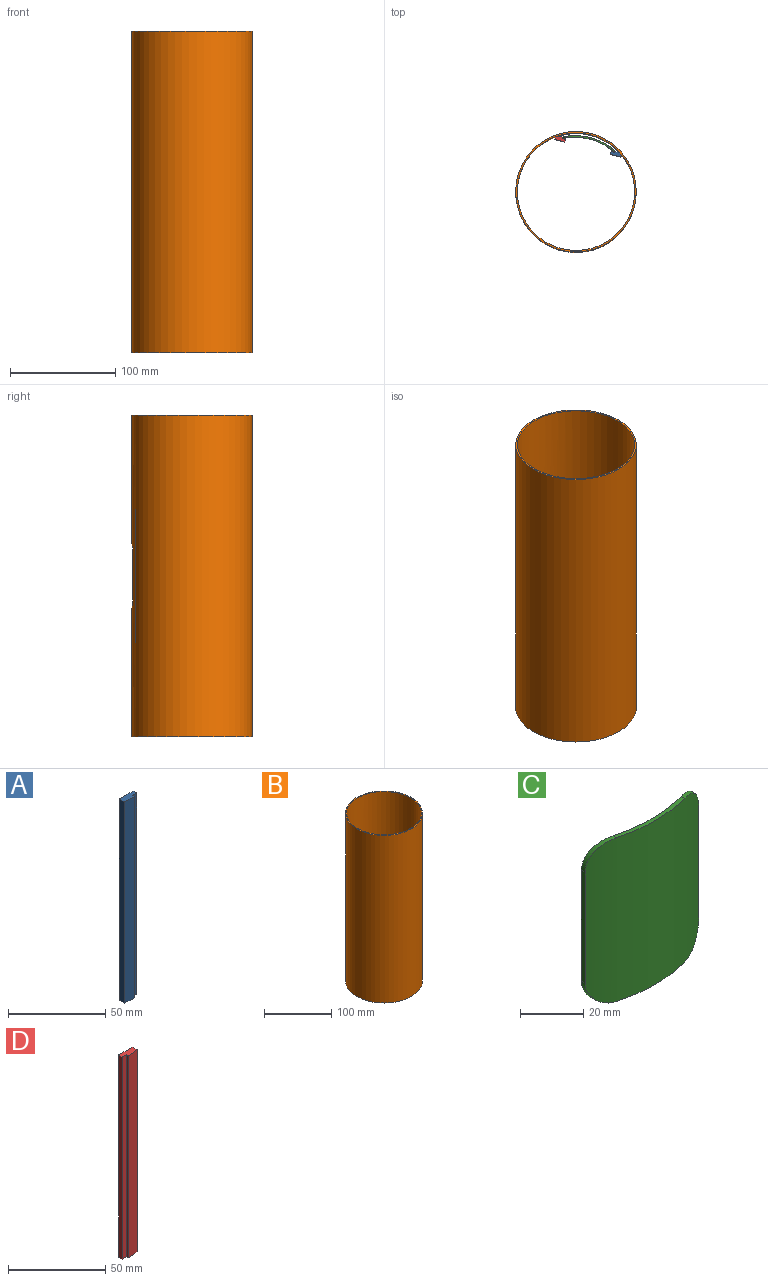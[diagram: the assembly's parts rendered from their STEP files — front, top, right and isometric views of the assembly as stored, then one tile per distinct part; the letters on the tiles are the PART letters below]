
ASSEMBLY  parts=4 mates=3
PART A: 8 faces, bbox 10x4x127 mm
  f0: plane 127x2.5mm, normal (1,0,0), area 317.5mm2, adj f1,f5,f6,f7
  f1: plane 127x10mm, normal (0,1,0), area 1270mm2, adj f0,f2,f6,f7
  f2: plane 127x3.56mm, normal (-1,0,0), area 451.9mm2, adj f1,f3,f6,f7
  f3: cylinder r=55.65mm len=127mm, axis (0,0,-1), area 891.4mm2, adj f2,f4,f6,f7
  f4: plane 127x1.5mm, normal (1,0,0), area 190.5mm2, adj f3,f5,f6,f7
  f5: plane 127x3mm, normal (0,-1,0), area 381mm2, adj f0,f4,f6,f7
  f6: plane 10x4mm, normal (0,0,1), area 34.5mm2, adj f0,f1,f2,f3,f4,f5
  f7: plane 10x4mm, normal (0,0,-1), area 34.5mm2, adj f0,f1,f2,f3,f4,f5
PART B: 12 faces, bbox 114.3x114.3x304.8 mm
  f0: cylinder r=55.65mm len=304.8mm, axis (0,0,-1), area 103323.9mm2, adj f2,f3,f4,f5,f6,f7,f8,f9
  f1: cylinder r=57.15mm len=304.8mm, axis (0,0,-1), area 106203.1mm2, adj f2,f3,f4,f5,f6,f7,f8,f9
  f2: plane 114.3x114.3mm, normal (0,0,1), area 531.6mm2, adj f0,f1
  f3: plane 114.3x114.3mm, normal (0,0,-1), area 531.6mm2, adj f0,f1
  f4: plane 30.48x3.63mm, normal (0,0,-1), area 46.3mm2, adj f0,f1,f5,f11
  f5: cylinder r=10.16mm len=10.16mm, axis (0,-1,0), area 26mm2, adj f0,f1,f4,f6
  f6: plane 43.18x1.68mm, normal (1,0,0), area 72.5mm2, adj f0,f1,f5,f7
  f7: cylinder r=10.16mm len=10.16mm, axis (0,-1,0), area 26mm2, adj f0,f1,f6,f8
  f8: plane 30.48x3.63mm, normal (0,0,1), area 46.3mm2, adj f0,f1,f7,f9
  f9: cylinder r=10.16mm len=10.16mm, axis (0,-1,0), area 26mm2, adj f0,f1,f8,f10
  f10: plane 43.18x1.68mm, normal (-1,0,0), area 72.5mm2, adj f0,f1,f9,f11
  f11: cylinder r=10.16mm len=10.16mm, axis (0,-1,0), area 26mm2, adj f0,f1,f4,f10
PART C: 10 faces, bbox 50.8x7.6x63.5 mm
  f0: plane 30.48x3.63mm, normal (0,0,1), area 46.3mm2, adj f2,f7,f8,f9
  f1: plane 30.48x3.63mm, normal (0,0,-1), area 46.3mm2, adj f4,f5,f8,f9
  f2: cylinder r=10.16mm len=10.16mm, axis (0,-1,0), area 26mm2, adj f0,f3,f8,f9
  f3: plane 43.18x1.68mm, normal (-1,0,0), area 72.5mm2, adj f2,f4,f8,f9
  f4: cylinder r=10.16mm len=10.16mm, axis (0,-1,0), area 26mm2, adj f1,f3,f8,f9
  f5: cylinder r=10.16mm len=10.16mm, axis (0,-1,0), area 26mm2, adj f1,f6,f8,f9
  f6: plane 43.18x1.68mm, normal (1,0,0), area 72.5mm2, adj f5,f7,f8,f9
  f7: cylinder r=10.16mm len=10.16mm, axis (0,-1,0), area 26mm2, adj f0,f6,f8,f9
  f8: cylinder r=55.65mm len=63.5mm, axis (0,0,-1), area 3252.3mm2, adj f0,f1,f2,f3,f4,f5,f6,f7
  f9: cylinder r=57.15mm len=63.5mm, axis (0,0,-1), area 3245.7mm2, adj f0,f1,f2,f3,f4,f5,f6,f7
PART D: 8 faces, bbox 10x4x127 mm
  f0: plane 127x1.5mm, normal (-1,0,0), area 190.5mm2, adj f1,f5,f6,f7
  f1: cylinder r=55.65mm len=127mm, axis (0,0,-1), area 891.4mm2, adj f0,f2,f6,f7
  f2: plane 127x3.56mm, normal (1,0,0), area 451.9mm2, adj f1,f3,f6,f7
  f3: plane 127x10mm, normal (0,1,0), area 1270mm2, adj f2,f4,f6,f7
  f4: plane 127x2.5mm, normal (-1,0,0), area 317.5mm2, adj f3,f5,f6,f7
  f5: plane 127x3mm, normal (0,-1,0), area 381mm2, adj f0,f4,f6,f7
  f6: plane 10x4mm, normal (0,0,1), area 34.5mm2, adj f0,f1,f2,f3,f4,f5
  f7: plane 10x4mm, normal (0,0,-1), area 34.5mm2, adj f0,f1,f2,f3,f4,f5
PLACE A rot(axis=(0,0,1),165deg) t=(5.35,115.38,13.28)mm
PLACE B rot(axis=(0,0,-1),15deg) t=(-3.9,69.24,-75.62)mm
PLACE C rot(axis=(0,0,1),165deg) t=(26.91,184.25,-75.62)mm
PLACE D rot(axis=(0,0,1),165deg) t=(11.15,113.83,13.28)mm
MATE fastened B.f4 <-> C.f0  axis (0,0,-1) through (-4.77,124.88,108.53)mm
MATE fastened D.f0 <-> C.f6  axis (0.97,-0.26,0) through (-16.48,120.45,76.78)mm
MATE fastened C.f3 <-> A.f4  axis (0.97,-0.26,0) through (32.46,106.81,76.78)mm
